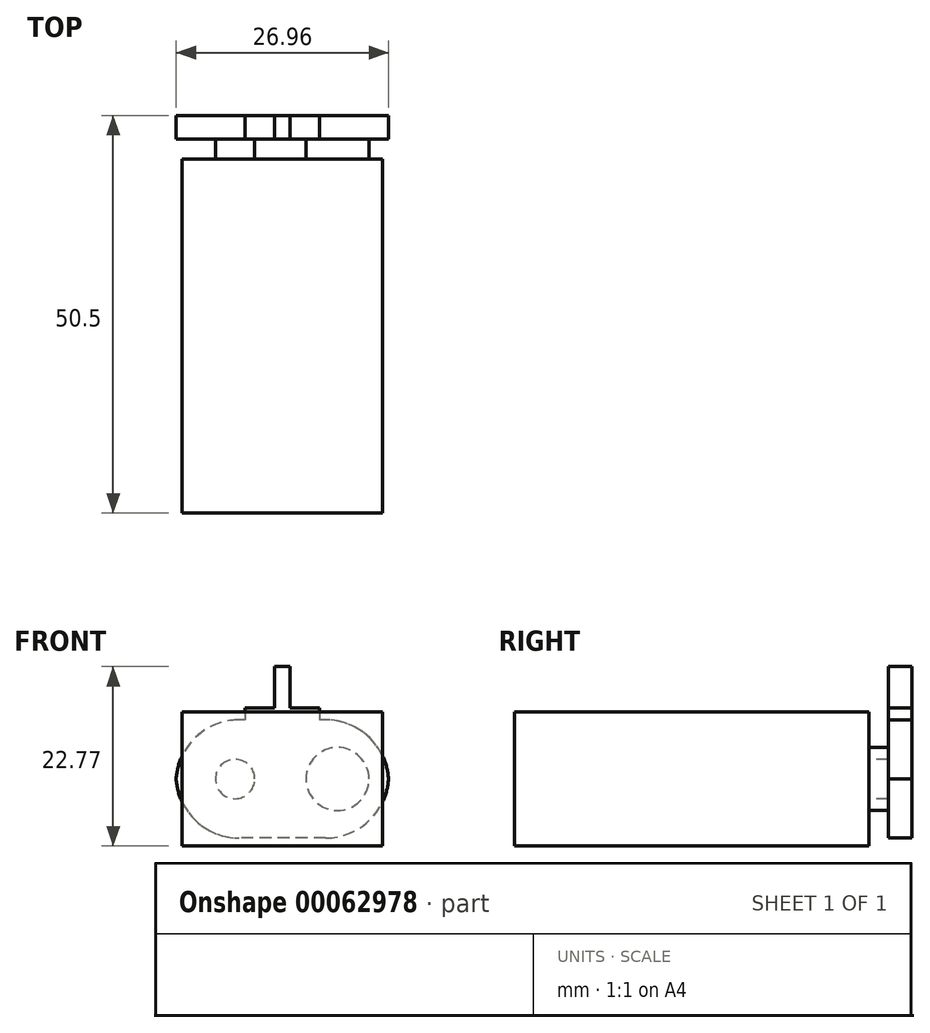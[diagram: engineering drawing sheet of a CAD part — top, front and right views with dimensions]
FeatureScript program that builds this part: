
annotation { "Feature Type Name" : "Feature", "Feature Type Description" : "" }
export const myFeature = defineFeature(function(context is Context, id is Id, definition is map)
    precondition{}
    {
        {
            var Q0;
            Q0=qCreatedBy(makeId("Top.planeOp"),FACE);
            var sketch = newSketch(context, id + "F0", { "sketchPlane" : qUnion([Q0])});
            skLineSegment(sketch, "E0.bottom", {"start": v(-12.75, 21.11) * mm, "end": v(12.75, 21.11) * mm});
            skLineSegment(sketch, "E0.top", {"start": v(-12.75, -23.89) * mm, "end": v(12.75, -23.89) * mm});
            skLineSegment(sketch, "E0.left", {"start": v(-12.75, 21.11) * mm, "end": v(-12.75, -23.89) * mm});
            skLineSegment(sketch, "E0.right", {"start": v(12.75, 21.11) * mm, "end": v(12.75, -23.89) * mm});
            skSolve(sketch);
        }
        {
            var Q0;
            Q0 = qSketchRegion(id + "F0", true);
            extrude(context, id + "F1", {"entities" : qUnion([Q0]), "endBound" : BoundingType.SYMMETRIC, "depth" : 17 * mm});
        }
        {
            var Q0;
            Q0=makeQuery(id+"F1.opExtrude","SWEPT_FACE",FACE,{"disambiguationData":[OSD([sQuery(id+"F0.wireOp",EDGE,"E0.bottom")])]});
            var sketch = newSketch(context, id + "F2", { "sketchPlane" : qUnion([Q0])});
            skCircle(sketch, "E1", {"center": v(6, 0) * mm, "radius": 2.5 * mm});
            skCircle(sketch, "E2", {"center": v(-7, 0) * mm, "radius": 4 * mm});
            skSolve(sketch);
        }
        {
            var Q0;
            Q0 = qSketchRegion(id + "F2", true);
            extrude(context, id + "F3", {"entities" : qUnion([Q0]), "operationType" : NewBodyOperationType.ADD, "depth" : 2.5 * mm});
        }
        {
            var Q0;
            Q0=makeQuery(id+"F3.opExtrude","CAP_FACE",FACE,{"disambiguationData":[OSD([sQuery(id+"F2.wireOp",EDGE,"E2")])],"isStart":false});
            var sketch = newSketch(context, id + "F4", { "sketchPlane" : qUnion([Q0])});
            skLineSegment(sketch, "E3.bottom", {"start": v(-13.5, 7.5) * mm, "end": v(-4.75, 7.5) * mm});
            skLineSegment(sketch, "E3.top", {"start": v(-13.5, -7.5) * mm, "end": v(13.5, -7.5) * mm});
            skLineSegment(sketch, "E3.left", {"start": v(-13.5, 7.5) * mm, "end": v(-13.5, -7.5) * mm});
            skLineSegment(sketch, "E3.right", {"start": v(13.5, 7.5) * mm, "end": v(13.5, -7.5) * mm});
            skLineSegment(sketch, "E4.bottom", {"start": v(-4.75, 9) * mm, "end": v(-1, 9) * mm});
            skLineSegment(sketch, "E4.left", {"start": v(-4.75, 9) * mm, "end": v(-4.75, 7.5) * mm});
            skLineSegment(sketch, "E4.right", {"start": v(4.75, 9) * mm, "end": v(4.75, 7.5) * mm});
            skLineSegment(sketch, "E5.trimOffspring", {"start": v(4.75, 7.5) * mm, "end": v(13.5, 7.5) * mm});
            skLineSegment(sketch, "E6.bottom", {"start": v(-1, 14.27) * mm, "end": v(1, 14.27) * mm});
            skLineSegment(sketch, "E6.left", {"start": v(-1, 14.27) * mm, "end": v(-1, 9) * mm});
            skLineSegment(sketch, "E6.right", {"start": v(1, 14.27) * mm, "end": v(1, 9) * mm});
            skLineSegment(sketch, "E7.trimOffspring", {"start": v(1, 9) * mm, "end": v(4.75, 9) * mm});
            skSolve(sketch);
        }
        {
            var Q0;
            Q0 = qSketchRegion(id + "F4", true);
            extrude(context, id + "F5", {"entities" : qUnion([Q0]), "operationType" : NewBodyOperationType.ADD, "depth" : 3 * mm});
        }
        {
            var Q0;
            Q0=makeQuery(id+"F5.opExtrude","SWEPT_EDGE",EDGE,{"disambiguationData":[OSD([sQuery(id+"F4.wireOp",EDGE,"E3.bottom"),sQuery(id+"F4.wireOp",EDGE,"E3.left")])]});
            var Q1;
            Q1=makeQuery(id+"F5.opExtrude","SWEPT_EDGE",EDGE,{"disambiguationData":[OSD([sQuery(id+"F4.wireOp",EDGE,"E3.right"),sQuery(id+"F4.wireOp",EDGE,"E5.trimOffspring")])]});
            var Q2;
            Q2=makeQuery(id+"F5.opExtrude","SWEPT_EDGE",EDGE,{"disambiguationData":[OSD([sQuery(id+"F4.wireOp",EDGE,"E3.top"),sQuery(id+"F4.wireOp",EDGE,"E3.right")])]});
            var Q3;
            Q3=makeQuery(id+"F5.opExtrude","SWEPT_EDGE",EDGE,{"disambiguationData":[OSD([sQuery(id+"F4.wireOp",EDGE,"E3.top"),sQuery(id+"F4.wireOp",EDGE,"E3.left")])]});
            fillet(context, id + "F6", {"entities" : qUnion([Q0, Q1, Q2, Q3]), "radius" : 8 * mm, "tangentPropagation" : true, "allowEdgeOverflow" : false});
        }
    });
